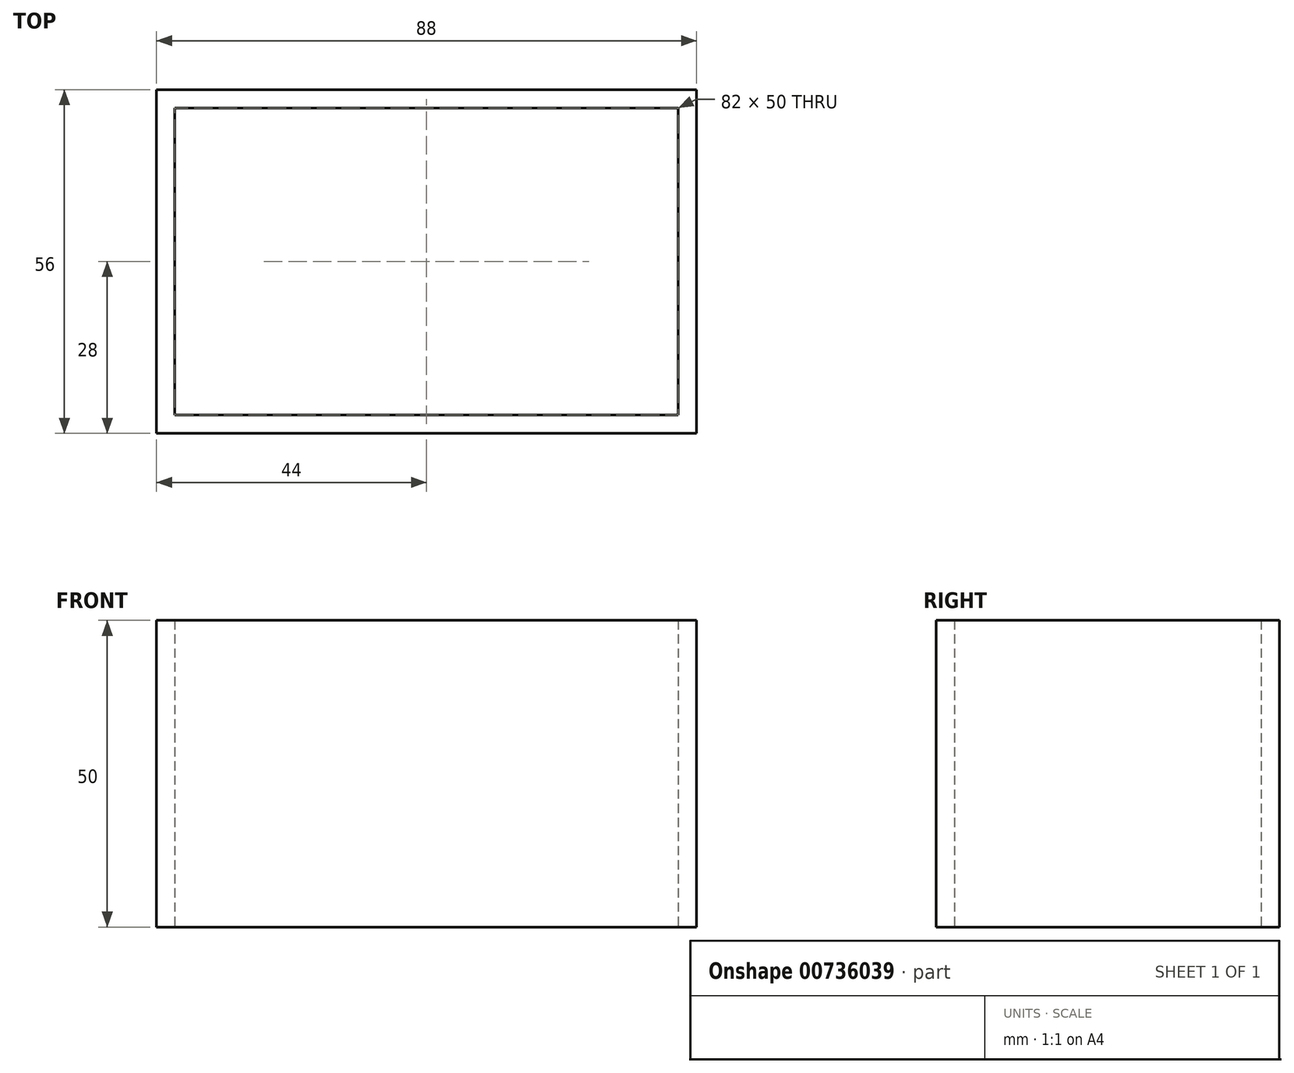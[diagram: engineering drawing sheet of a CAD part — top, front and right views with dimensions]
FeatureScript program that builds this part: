
annotation { "Feature Type Name" : "Feature", "Feature Type Description" : "" }
export const myFeature = defineFeature(function(context is Context, id is Id, definition is map)
    precondition{}
    {
        {
            var Q0;
            Q0=qCreatedBy(makeId("Top.planeOp"),FACE);
            var sketch = newSketch(context, id + "F0", { "sketchPlane" : qUnion([Q0])});
            skLineSegment(sketch, "E0.bottom", {"start": v(41, -25) * mm, "end": v(-41, -25) * mm});
            skLineSegment(sketch, "E0.top", {"start": v(41, 25) * mm, "end": v(-41, 25) * mm});
            skLineSegment(sketch, "E0.left", {"start": v(41, -25) * mm, "end": v(41, 25) * mm});
            skLineSegment(sketch, "E0.right", {"start": v(-41, -25) * mm, "end": v(-41, 25) * mm});
            skPoint(sketch, "E0.middle", {"position": v(0, 0) * mm});
            skLineSegment(sketch, "E1.bottom", {"start": v(44, -28) * mm, "end": v(-44, -28) * mm});
            skLineSegment(sketch, "E1.top", {"start": v(44, 28) * mm, "end": v(-44, 28) * mm});
            skLineSegment(sketch, "E1.left", {"start": v(44, -28) * mm, "end": v(44, 28) * mm});
            skLineSegment(sketch, "E1.right", {"start": v(-44, -28) * mm, "end": v(-44, 28) * mm});
            skSolve(sketch);
        }
        {
            var Q0;
            Q0=makeQuery(id+"F0.imprint","IMPRINT",FACE,{"disambiguationData":[TD([[makeQuery(id+"F0.imprint","IMPRINT",EDGE,{"derivedFrom":sQuery(id+"F0.wireOp",EDGE,"E0.bottom")}),1.0]])]});
            extrude(context, id + "F1", {"entities" : qUnion([Q0]), "depth" : 50 * mm, "offsetDistance" : 25.4 * mm});
        }
    });
